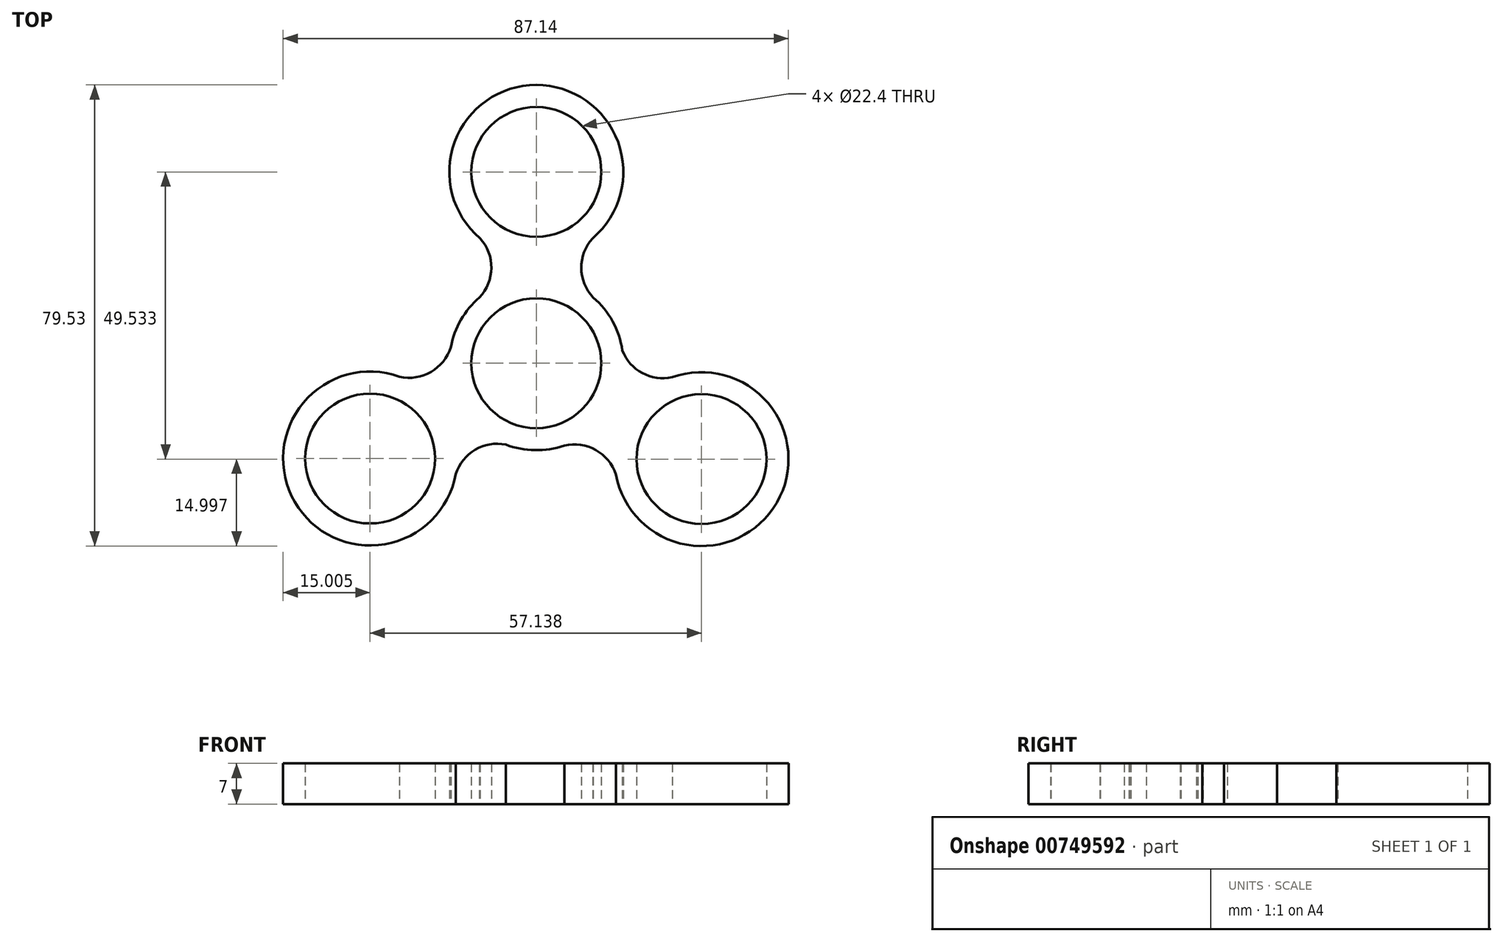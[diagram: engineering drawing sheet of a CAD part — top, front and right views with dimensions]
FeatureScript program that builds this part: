
annotation { "Feature Type Name" : "Feature", "Feature Type Description" : "" }
export const myFeature = defineFeature(function(context is Context, id is Id, definition is map)
    precondition{}
    {
        {
            var Q0;
            Q0=qCreatedBy(makeId("Top.planeOp"),FACE);
            var sketch = newSketch(context, id + "F0", { "sketchPlane" : qUnion([Q0])});
            skCircle(sketch, "E0", {"center": v(0, 28.26) * mm, "radius": 11.2 * mm});
            skCircle(sketch, "E1", {"center": v(0, -4.74) * mm, "radius": 11.2 * mm});
            skArc(sketch, "E2", {"start": v(9.7, 16.82) * mm, "mid": v(0, 43.26) * mm, "end": v(-9.7, 16.82) * mm});
            skArc(sketch, "E3", {"start": v(-9.81, 6.6) * mm, "mid": v(0, -19.74) * mm, "end": v(9.81, 6.6) * mm});
            skArc(sketch, "E4", {"start": v(9.7, 16.82) * mm, "mid": v(7.75, 11.7) * mm, "end": v(9.81, 6.6) * mm});
            skArc(sketch, "E5", {"start": v(-9.81, 6.6) * mm, "mid": v(-7.75, 11.7) * mm, "end": v(-9.7, 16.82) * mm});
            skArc(sketch, "E6.1.0", {"start": v(-23.6, -7.05) * mm, "mid": v(-41.65, -28.67) * mm, "end": v(-13.9, -23.86) * mm});
            skCircle(sketch, "E6.1.1", {"center": v(-28.66, -21.17) * mm, "radius": 11.2 * mm});
            skArc(sketch, "E6.1.3", {"start": v(-5, -18.84) * mm, "mid": v(-10.43, -19.6) * mm, "end": v(-13.9, -23.86) * mm});
            skArc(sketch, "E6.2.0", {"start": v(13.72, -23.96) * mm, "mid": v(41.47, -28.77) * mm, "end": v(23.43, -7.15) * mm});
            skCircle(sketch, "E6.2.1", {"center": v(28.48, -21.27) * mm, "radius": 11.2 * mm});
            skArc(sketch, "E6.2.2", {"start": v(13.72, -23.96) * mm, "mid": v(10.26, -19.7) * mm, "end": v(4.82, -18.94) * mm});
            skArc(sketch, "E6.2.3", {"start": v(14.64, -1.95) * mm, "mid": v(18, -6.28) * mm, "end": v(23.43, -7.15) * mm});
            skPoint(sketch, "E6.center", {"position": v(-0.06, -4.73) * mm});
            skArc(sketch, "E7", {"start": v(-23.6, -7.05) * mm, "mid": v(-18.16, -6.24) * mm, "end": v(-14.74, -1.95) * mm});
            skSolve(sketch);
        }
        {
            var Q0;
            Q0=makeQuery(id+"F0.imprint","IMPRINT",FACE,{"disambiguationData":[TD([[makeQuery(id+"F0.imprint","IMPRINT",EDGE,{"derivedFrom":sQuery(id+"F0.wireOp",EDGE,"E0")}),-1.0]])]});
            extrude(context, id + "F1", {"entities" : qUnion([Q0]), "depth" : 7 * mm, "offsetDistance" : 25 * mm});
        }
        {
            var Q0;
            Q0=qSketchRegion(id+"F0",true);
            extrude(context, id + "F2", {"entities" : qUnion([Q0]), "operationType" : NewBodyOperationType.ADD, "depth" : 7 * mm, "offsetDistance" : 25 * mm});
        }
    });
